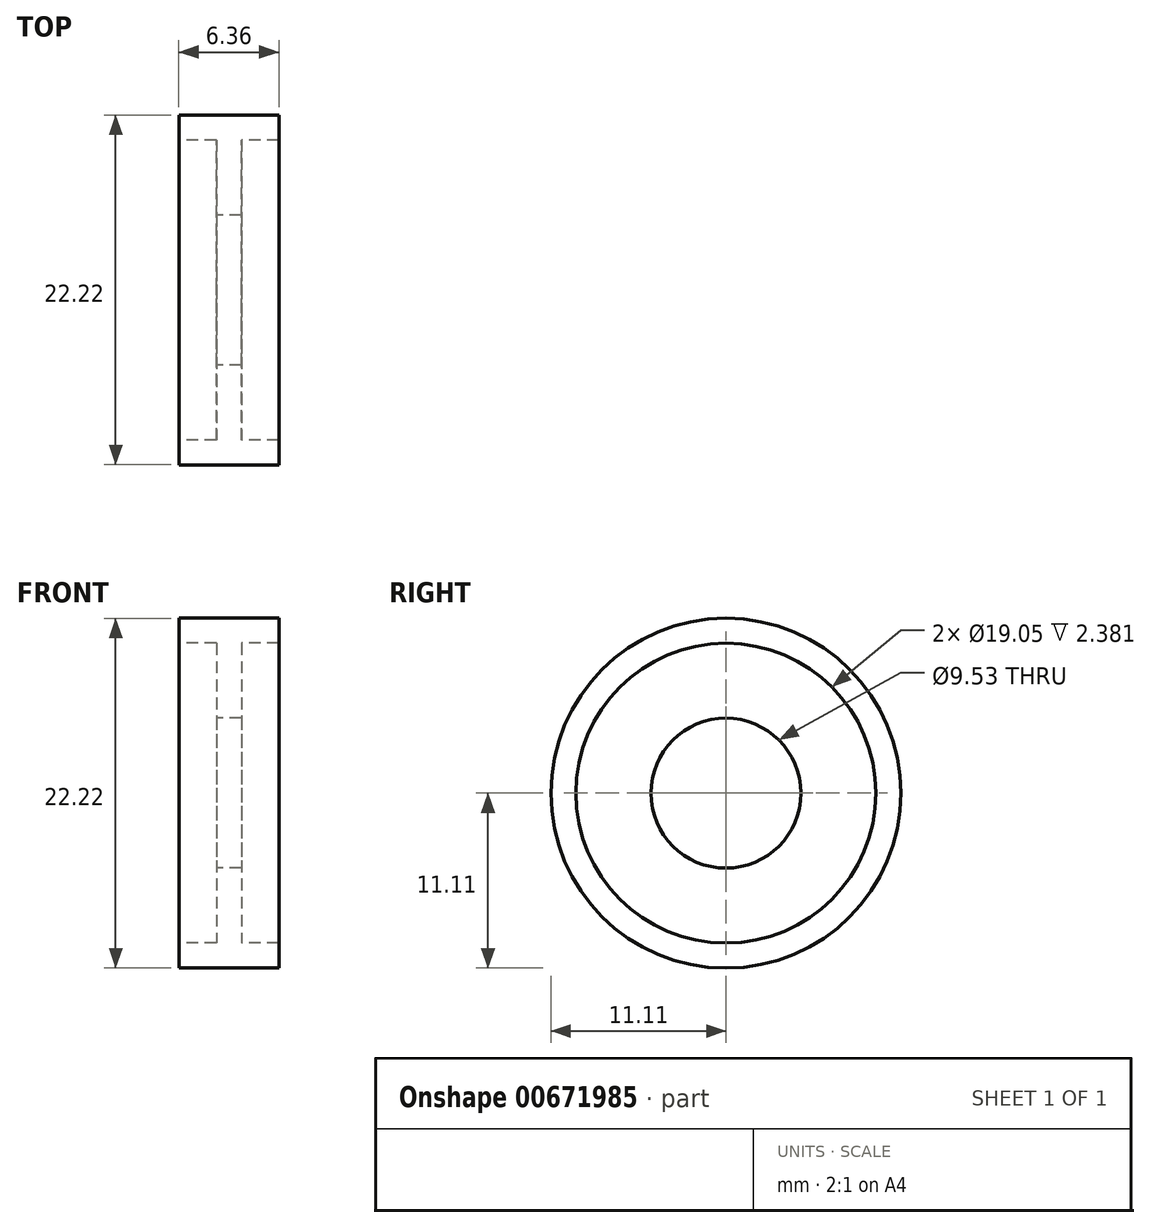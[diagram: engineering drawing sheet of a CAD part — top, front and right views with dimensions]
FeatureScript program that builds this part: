
annotation { "Feature Type Name" : "Feature", "Feature Type Description" : "" }
export const myFeature = defineFeature(function(context is Context, id is Id, definition is map)
    precondition{}
    {
        {
            var Q0;
            Q0=qCreatedBy(makeId("Front.planeOp"),FACE);
            var sketch = newSketch(context, id + "F0", { "sketchPlane" : qUnion([Q0])});
            skLineSegment(sketch, "E0", {"start": v(-44.48, 0) * mm, "end": v(53.44, 0) * mm, "construction": true});
            skLineSegment(sketch, "E1", {"start": v(0, 4.76) * mm, "end": v(-0.8, 4.76) * mm});
            skLineSegment(sketch, "E2", {"start": v(-3.18, 11.11) * mm, "end": v(0, 11.11) * mm});
            skLineSegment(sketch, "E3", {"start": v(0, 11.11) * mm, "end": v(0, 0) * mm, "construction": true});
            skLineSegment(sketch, "E4", {"start": v(-0.8, 4.76) * mm, "end": v(-0.8, 9.53) * mm});
            skLineSegment(sketch, "E5", {"start": v(-3.18, 11.11) * mm, "end": v(-3.18, 9.53) * mm});
            skLineSegment(sketch, "E6", {"start": v(-3.18, 9.53) * mm, "end": v(-0.8, 9.53) * mm});
            skLineSegment(sketch, "E7.MirrorCS", {"start": v(3.18, 11.11) * mm, "end": v(0, 11.11) * mm});
            skLineSegment(sketch, "E8.MirrorCS", {"start": v(3.18, 11.11) * mm, "end": v(3.18, 9.53) * mm});
            skLineSegment(sketch, "E9.MirrorCS", {"start": v(0.8, 4.76) * mm, "end": v(0.8, 9.53) * mm});
            skLineSegment(sketch, "E10.MirrorCS", {"start": v(3.18, 9.53) * mm, "end": v(0.8, 9.53) * mm});
            skLineSegment(sketch, "E11.MirrorCS", {"start": v(0, 4.76) * mm, "end": v(0.8, 4.76) * mm});
            skLineSegment(sketch, "E12", {"start": v(0, 0) * mm, "end": v(0, 4.76) * mm, "construction": true});
            skSolve(sketch);
        }
        {
            var Q0;
            Q0=makeQuery(id+"F0.imprint","IMPRINT",FACE,{"disambiguationData":[TD([[makeQuery(id+"F0.imprint","IMPRINT",EDGE,{"derivedFrom":sQuery(id+"F0.wireOp",EDGE,"E1")}),-1.0]])]});
            var Q1;
            Q1=sQuery(id+"F0.wireOp",EDGE,"E0");
            revolve(context, id + "F1", {"entities" : qUnion([Q0]), "axis" : qUnion([Q1]), "revolveType" : RevolveType.FULL});
        }
    });
